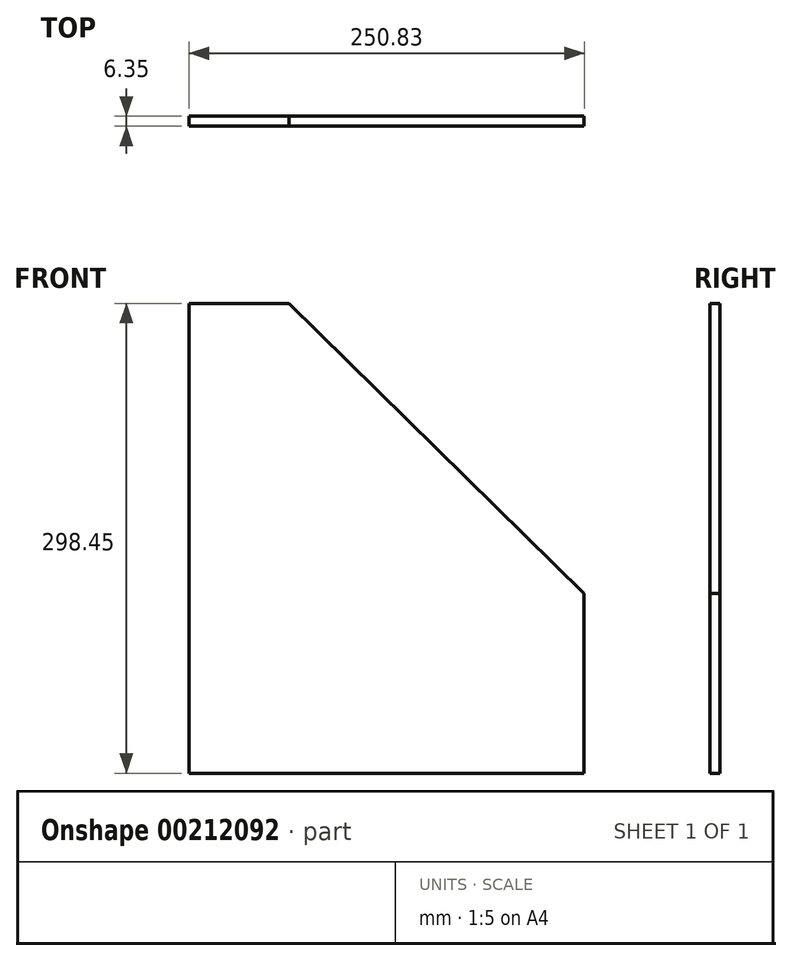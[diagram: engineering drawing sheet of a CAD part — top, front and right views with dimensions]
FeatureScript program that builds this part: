
annotation { "Feature Type Name" : "Feature", "Feature Type Description" : "" }
export const myFeature = defineFeature(function(context is Context, id is Id, definition is map)
    precondition{}
    {
        {
            var Q0;
            Q0=qCreatedBy(makeId("Front.planeOp"),FACE);
            var sketch = newSketch(context, id + "F0", { "sketchPlane" : qUnion([Q0])});
            skLineSegment(sketch, "E0.bottom", {"start": v(0, 0) * mm, "end": v(250.82, 0) * mm});
            skLineSegment(sketch, "E0.top", {"start": v(0, 298.45) * mm, "end": v(63.5, 298.45) * mm});
            skLineSegment(sketch, "E0.left", {"start": v(0, 0) * mm, "end": v(0, 298.45) * mm});
            skLineSegment(sketch, "E0.right", {"start": v(250.83, 0) * mm, "end": v(250.83, 114.3) * mm});
            skLineSegment(sketch, "E1", {"start": v(63.5, 298.45) * mm, "end": v(250.83, 114.3) * mm});
            skSolve(sketch);
        }
        {
            var Q0;
            Q0 = qSketchRegion(id + "F0", true);
            extrude(context, id + "F1", {"entities" : qUnion([Q0]), "depth" : 6.35 * mm});
        }
    });
